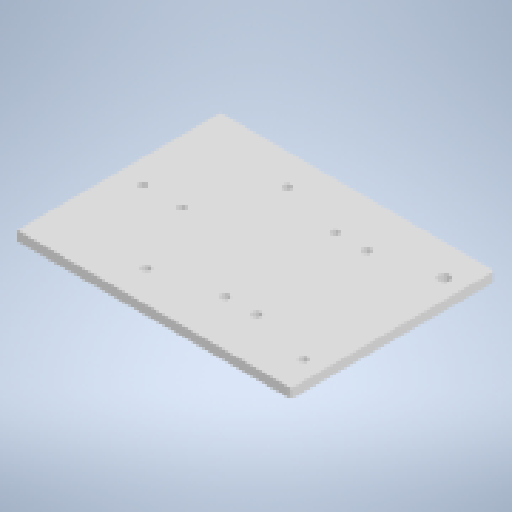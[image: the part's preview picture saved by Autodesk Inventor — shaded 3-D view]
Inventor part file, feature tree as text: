
AUTODESK INVENTOR PART (.ipt)
format: ipt  version: 2023.2 (Build 272271000, 271)  size: 171,008 bytes
history: native  units: mm
features: reference x4, other x4, sketch x3, hole x2, extrude x1, fillet x1
ambient origin geometry x8: Origin, YZ Plane, XZ Plane, XY Plane, X Axis, Y Axis, Z Axis, Center Point
bodies: Solid1 (feature_tree)
feature tree (15):
  extrude  "Extrusion1"  Depth=6.0mm
  fillet  "Fillet1"  Radius=6.0mm
  hole  "Hole1"  [1 undecoded]
  hole  "Hole2"  [1 undecoded]
  sketch  "Sketch1"  dims[d0=125.0mm d1=130.0mm d2=12.3mm d3=12.3mm d4=5.1mm d5=5.1mm d6=5.1mm d7=7.1mm d8=50.0mm d9=6.0mm d10=0.0mm]
  sketch  "Sketch2"  dims[d11=2.0mm d12=10.0mm]
  sketch  "Sketch3"  dims[d13=10.0mm d14=15.0mm d15=25.0mm d16=5.1mm d17=6.0mm d18=4.0mm d19=2.0mm d20=90.0deg d21=8.0mm d22=20.594885mm d23=20.0mm d24=20.0mm d25=20.0mm d26=20.0mm d27=5.1mm d28=6.0mm d29=4.0mm d30=2.0mm d31=90.0deg d32=8.0mm d33=20.594885mm]
  reference  "Reference1"
  reference  "Reference2"
  reference  "Reference3"
  reference  "Reference4"
  parser-record x1  (decoder bookkeeping rows leaked as tree rows — omitted from the tree; the rows remain in map.json)
  other  "Main Assembly.iam"
  other  "ACME-Nut-Block:1"
  other  "ACME-Nut-Block:2"
note: 2 required parameter values undecoded (feature->parameter linkage not recoverable at this tier; creation-order binding heuristic only, values carry confidence <= 0.55)
note: 1 file-system path scrubbed to <path> (originals preserved in map.json)
